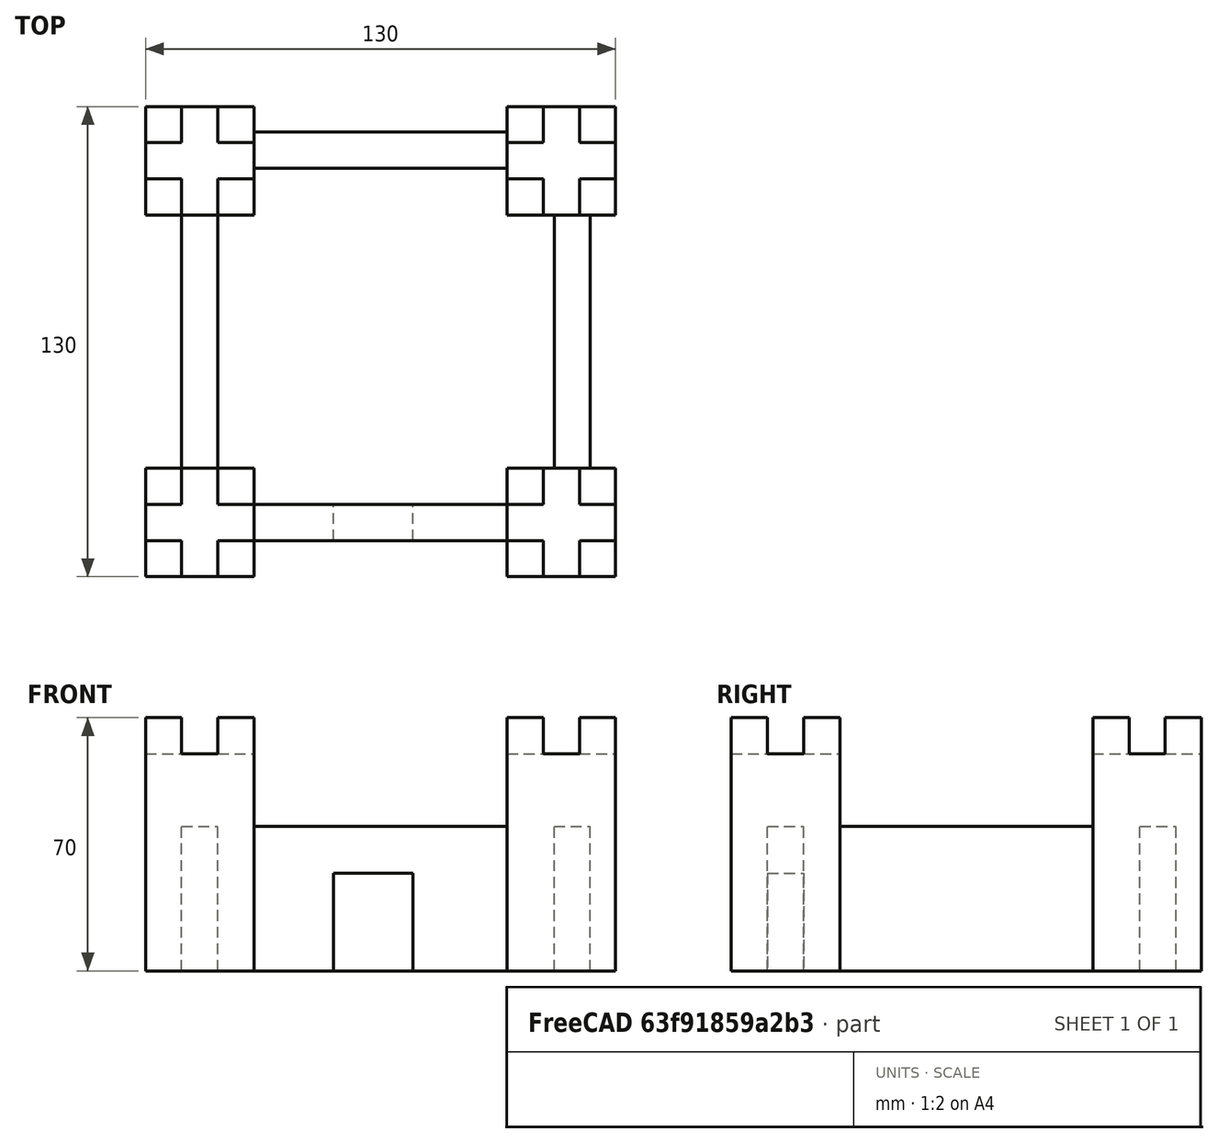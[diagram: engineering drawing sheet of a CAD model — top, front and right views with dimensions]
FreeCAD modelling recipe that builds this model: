
FCSTD DOCUMENT  (FreeCAD 0.16R6707 (Git))
Label: 03-Castillo-basico
License: All rights reserved
LicenseURL: http://en.wikipedia.org/wiki/All_rights_reserved
objects: Part::Feature×8, Part::Box×5, Part::MultiFuse×2, Part::Cut×1
note: 16 computed .brp shape members not serialized (recipe doc carries the construction recipe); baked Part::Feature solids carry a one-line shape summary decoded from their .brp

FEATURE [Part::Box] Box  label="Torre_base"
  Height = 60
  Length = 30
  Width = 30
FEATURE [Part::Box] Box001  label="Almena"
  Height = 10
  Length = 10
  Placement = pos=(0,0,60) rot=(0,0,1;0rad)
  Width = 10
FEATURE [Part::Feature] Box001001  label="Almena001"
  Placement = pos=(20,0,60) rot=(0,0,1;0rad)
  shape: bbox 10 x 10 x 10 mm, 6 faces (baked)
FEATURE [Part::Feature] Box001002  label="Almena002"
  Placement = pos=(0,20,60) rot=(0,0,1;0rad)
  shape: bbox 10 x 10 x 10 mm, 6 faces (baked)
FEATURE [Part::Feature] Box001002001  label="Almena003"
  Placement = pos=(20,20,60) rot=(0,0,1;0rad)
  shape: bbox 10 x 10 x 10 mm, 6 faces (baked)
FEATURE [Part::MultiFuse] Fusion  label="Torre"
  Shapes = -> [Box,Box001002,Box001001,Box001002001,Box001]
FEATURE [Part::Feature] Fusion001  label="Torre001"
  Placement = pos=(100,0,0) rot=(0,0,1;0rad)
  shape: bbox 30 x 30 x 70 mm, 18 faces (baked)
FEATURE [Part::Feature] Fusion002  label="Torre002"
  Placement = pos=(0,100,0) rot=(0,0,1;0rad)
  shape: bbox 30 x 30 x 70 mm, 18 faces (baked)
FEATURE [Part::Feature] Fusion001001  label="Torre003"
  Placement = pos=(100,100,0) rot=(0,0,1;0rad)
  shape: bbox 30 x 30 x 70 mm, 18 faces (baked)
FEATURE [Part::Box] Box001002002  label="Muro-frontal"
  Height = 40
  Length = 70
  Placement = pos=(30,10,0) rot=(0,0,1;0rad)
  Width = 10
FEATURE [Part::Feature] Box001002002001  label="Cubo001"
  Placement = pos=(30,113,0) rot=(0,0,1;0rad)
  shape: bbox 70 x 10 x 40 mm, 6 faces (baked)
FEATURE [Part::Box] Box001002002002  label="Cubo"
  Height = 40
  Length = 10
  Placement = pos=(10,30,0) rot=(0,0,1;0rad)
  Width = 70
FEATURE [Part::Feature] Box001002002002001  label="Cubo002"
  Placement = pos=(113,30,0) rot=(0,0,1;0rad)
  shape: bbox 10 x 70 x 40 mm, 6 faces (baked)
FEATURE [Part::MultiFuse] Fusion001002  label="Castillo-base"
  Shapes = -> [Fusion,Box001002002002,Fusion001001,Box001002002001,Fusion002,Fusion001,Box001002002,Box001002002002001]
FEATURE [Part::Box] Box001002002002002  label="Cubo003"
  Height = 30
  Length = 22
  Placement = pos=(52,0,-3) rot=(0,0,1;0rad)
  Width = 34
FEATURE [Part::Cut] Cut  label="Castillo-puerta"
  Base = -> Fusion001002
  Tool = -> Box001002002002002
